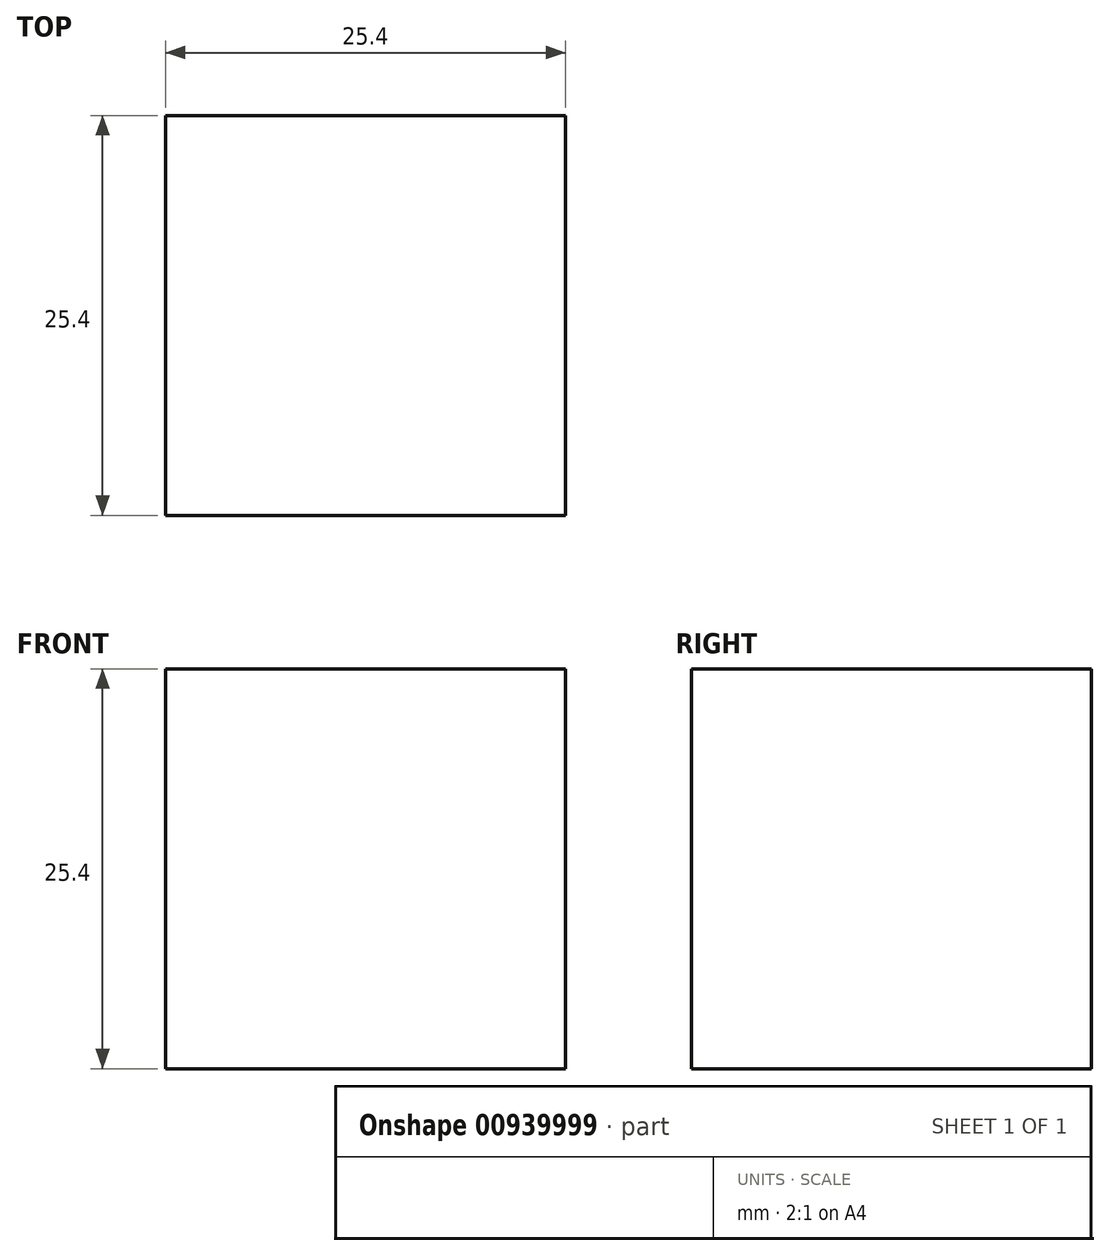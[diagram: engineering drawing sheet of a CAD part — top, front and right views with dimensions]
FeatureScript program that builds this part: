
annotation { "Feature Type Name" : "Feature", "Feature Type Description" : "" }
export const myFeature = defineFeature(function(context is Context, id is Id, definition is map)
    precondition{}
    {
        {
            var Q0;
            Q0=qCreatedBy(makeId("Top.planeOp"),FACE);
            var sketch = newSketch(context, id + "F0", { "sketchPlane" : qUnion([Q0])});
            skLineSegment(sketch, "E0", {"start": v(-29.67, 20.19) * mm, "end": v(-29.67, -5.21) * mm});
            skLineSegment(sketch, "E1", {"start": v(-29.67, -5.21) * mm, "end": v(-4.27, -5.21) * mm});
            skLineSegment(sketch, "E2", {"start": v(-4.27, -5.21) * mm, "end": v(-4.27, 20.19) * mm});
            skLineSegment(sketch, "E3", {"start": v(-4.27, 20.19) * mm, "end": v(-29.67, 20.19) * mm});
            skSolve(sketch);
        }
        {
            var Q0;
            Q0 = qSketchRegion(id + "F0", true);
            extrude(context, id + "F1", {"entities" : qUnion([Q0]), "depth" : 25.4 * mm, "offsetDistance" : 25.4 * mm});
        }
    });
